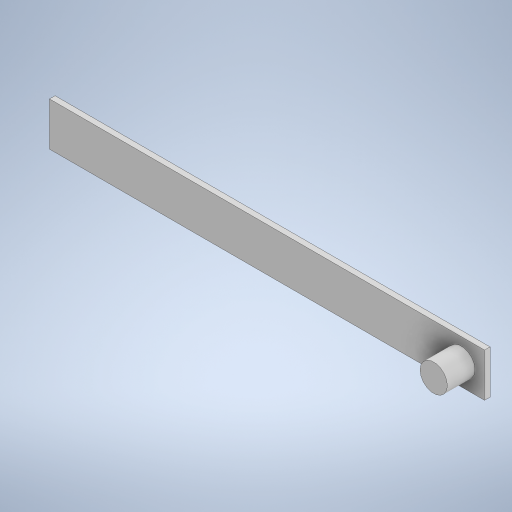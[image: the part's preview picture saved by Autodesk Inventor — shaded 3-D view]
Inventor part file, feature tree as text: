
AUTODESK INVENTOR PART (.ipt)
format: ipt  version: 2024 (Build 280153000, 153)  size: 236,032 bytes
history: native  units: in
note: dims shown in document units (in); Inventor stores cm internally (conversion verified against a paired STEP export)
features: extrude x2, sketch x2
ambient origin geometry x8: Origin, YZ Plane, XZ Plane, XY Plane, X Axis, Y Axis, Z Axis, Center Point
bodies: Solid1 (feature_tree)
feature tree (4):
  extrude  "Extrusion1"  Depth=7.874in
  extrude  "Extrusion2"  Depth=5.0in
  sketch  "Sketch1"  dims[d0=78.7402in d1=7.874in]
  sketch  "Sketch2"  dims[d2=1.0in d3=0.0in d4=4.9498in d5=74.6394in d6=5.0in d7=0.0in]
